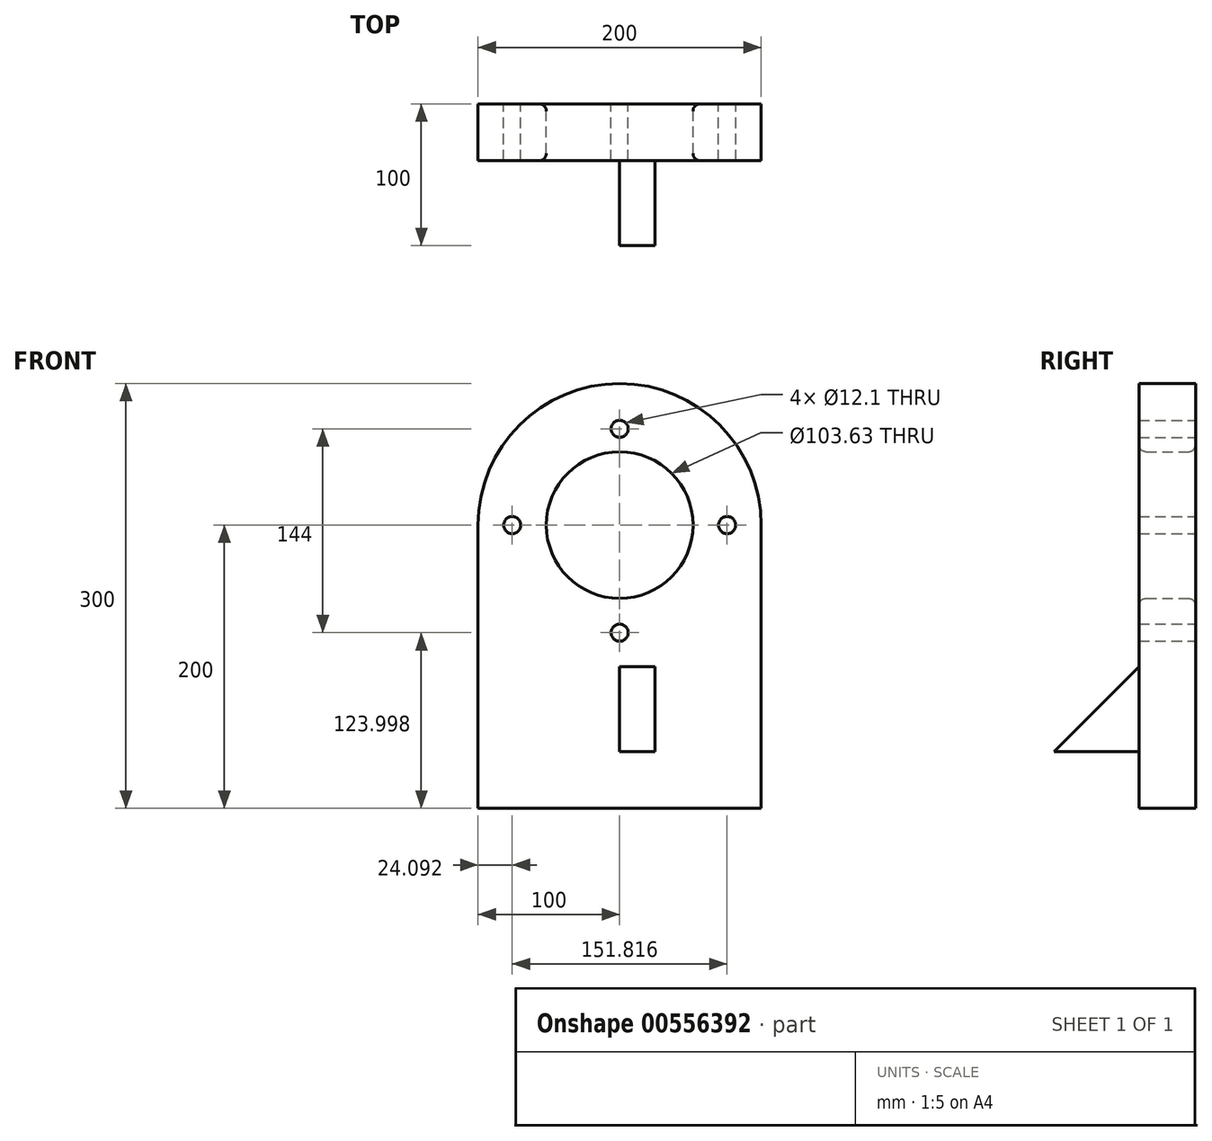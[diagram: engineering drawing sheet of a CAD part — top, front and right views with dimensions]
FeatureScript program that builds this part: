
annotation { "Feature Type Name" : "Feature", "Feature Type Description" : "" }
export const myFeature = defineFeature(function(context is Context, id is Id, definition is map)
    precondition{}
    {
        {
            var Q0;
            Q0=qCreatedBy(makeId("Front.planeOp"),FACE);
            var sketch = newSketch(context, id + "F0", { "sketchPlane" : qUnion([Q0])});
            skLineSegment(sketch, "E0.bottom", {"start": v(0, 0) * mm, "end": v(-100, 0) * mm});
            skLineSegment(sketch, "E0.top", {"start": v(-51.82, 200) * mm, "end": v(-100, 200) * mm});
            skLineSegment(sketch, "E0.left", {"start": v(0, 0) * mm, "end": v(0, 148.18) * mm});
            skLineSegment(sketch, "E0.right", {"start": v(-100, 0) * mm, "end": v(-100, 200) * mm});
            skLineSegment(sketch, "E1.MirrorCS", {"start": v(0, 0) * mm, "end": v(100, 0) * mm});
            skLineSegment(sketch, "E2.MirrorCS", {"start": v(100, 0) * mm, "end": v(100, 200) * mm});
            skLineSegment(sketch, "E3.MirrorCS", {"start": v(51.82, 200) * mm, "end": v(100, 200) * mm});
            skCircle(sketch, "E4", {"center": v(0, 200) * mm, "radius": 100 * mm});
            skCircle(sketch, "E5", {"center": v(0, 200) * mm, "radius": 51.82 * mm});
            skPoint(sketch, "E6", {"position": v(-75.9, 200) * mm});
            skPoint(sketch, "E7", {"position": v(0, 268) * mm});
            skPoint(sketch, "E8", {"position": v(75.9, 200) * mm});
            skPoint(sketch, "E9", {"position": v(0, 124) * mm});
            skLineSegment(sketch, "E10", {"start": v(0, 148.18) * mm, "end": v(0, 351.78) * mm});
            skSolve(sketch);
        }
        {
            var Q0;
            {var subQ0=sQuery(id+"F0.wireOp",EDGE,"E0.bottom");Q0=makeQuery(id+"F0.imprint","IMPRINT",FACE,{"disambiguationData":[TD([[makeQuery(id+"F0.imprint","IMPRINT",EDGE,{"derivedFrom":subQ0}),-1.0]])]});}
            var Q1;
            {var subQ0=sQuery(id+"F0.wireOp",EDGE,"E1.MirrorCS");Q1=makeQuery(id+"F0.imprint","IMPRINT",FACE,{"disambiguationData":[TD([[makeQuery(id+"F0.imprint","IMPRINT",EDGE,{"derivedFrom":subQ0}),1.0]])]});}
            var Q2;
            {var subQ0=sQuery(id+"F0.wireOp",EDGE,"E10");var subQ1=sQuery(id+"F0.wireOp",EDGE,"E0.left");var subQ2=makeQuery(id+"F0.imprint","INTERSECT",VERTEX,{"derivedFrom":[subQ1,subQ0]});Q2=makeQuery(id+"F0.imprint","IMPRINT",FACE,{"disambiguationData":[TD([[makeQuery(id+"F0.imprint","IMPRINT",EDGE,{"disambiguationData":[TD([[subQ2,1.0]])],"derivedFrom":subQ1}),1.0]])]});}
            var Q3;
            {var subQ0=sQuery(id+"F0.wireOp",EDGE,"E10");var subQ1=sQuery(id+"F0.wireOp",EDGE,"E0.left");var subQ2=makeQuery(id+"F0.imprint","INTERSECT",VERTEX,{"derivedFrom":[subQ1,subQ0]});Q3=makeQuery(id+"F0.imprint","IMPRINT",FACE,{"disambiguationData":[TD([[makeQuery(id+"F0.imprint","IMPRINT",EDGE,{"disambiguationData":[TD([[subQ2,1.0]])],"derivedFrom":subQ1}),-1.0]])]});}
            var Q4;
            {var subQ0=sQuery(id+"F0.wireOp",EDGE,"E0.top");Q4=makeQuery(id+"F0.imprint","IMPRINT",FACE,{"disambiguationData":[TD([[makeQuery(id+"F0.imprint","IMPRINT",EDGE,{"derivedFrom":subQ0}),-1.0]])]});}
            var Q5;
            {var subQ0=sQuery(id+"F0.wireOp",EDGE,"E3.MirrorCS");Q5=makeQuery(id+"F0.imprint","IMPRINT",FACE,{"disambiguationData":[TD([[makeQuery(id+"F0.imprint","IMPRINT",EDGE,{"derivedFrom":subQ0}),1.0]])]});}
            extrude(context, id + "F1", {"entities" : qUnion([Q0, Q1, Q2, Q3, Q4, Q5]), "depth" : 40 * mm, "offsetDistance" : 25 * mm});
        }
        {
            var Q0;
            Q0=sQuery(id+"F0.wireOp",VERTEX,"E6");
            var Q1;
            Q1=sQuery(id+"F0.wireOp",VERTEX,"E7");
            var Q2;
            Q2=sQuery(id+"F0.wireOp",VERTEX,"E8");
            var Q3;
            Q3=sQuery(id+"F0.wireOp",VERTEX,"E9");
            var Q4;
            Q4=makeQuery(id+"F1.opExtrude","SWEPT_BODY",BODY,{"disambiguationData":[OSD([sQuery(id+"F0.wireOp",EDGE,"E0.bottom"),sQuery(id+"F0.wireOp",EDGE,"E0.right"),sQuery(id+"F0.wireOp",EDGE,"E1.MirrorCS"),sQuery(id+"F0.wireOp",EDGE,"E2.MirrorCS"),sQuery(id+"F0.wireOp",EDGE,"E4")])]});
            hole(context, id + "F2", {"style" : HoleStyle.SIMPLE, "endStyle" : HoleEndStyle.THROUGH, "oppositeDirection" : true, "standardTappedOrClearance" : lookupTablePath({ "standard" : "ISO", "engagement" : "75%", "pitch" : "2 mm", "size" : "M14", "type" : "Tapped" }), "standardBlindInLast" : lookupTablePath({ "standard" : "ISO", "engagement" : "75%", "pitch" : "2 mm", "size" : "M14", "type" : "Tapped" }), "holeDiameter" : 12.1 * mm, "showTappedDepth" : true, "isTappedThrough" : true, "tappedDepth" : 12 * mm, "tapClearance" : 3, "locations" : qUnion([Q0, Q1, Q2, Q3]), "scope" : qUnion([Q4]), "majorDiameter" : 14 * mm});
        }
        {
            var Q0;
            Q0=makeQuery(id+"F1.opExtrude","CAP_EDGE",EDGE,{"disambiguationData":[OSD([sQuery(id+"F0.wireOp",EDGE,"E5")])],"isStart":false});
            fillet(context, id + "F3", {"entities" : qUnion([Q0]), "radius" : 5 * mm, "tangentPropagation" : true, "allowEdgeOverflow" : false});
        }
        {
            var Q0;
            Q0=makeQuery(id+"F1.opExtrude","CAP_EDGE",EDGE,{"disambiguationData":[OSD([sQuery(id+"F0.wireOp",EDGE,"E5")])],"isStart":true});
            fillet(context, id + "F4", {"entities" : qUnion([Q0]), "radius" : 5 * mm, "tangentPropagation" : true, "allowEdgeOverflow" : false});
        }
        {
            var Q0;
            Q0=qCreatedBy(makeId("Right.planeOp"),FACE);
            var sketch = newSketch(context, id + "F5", { "sketchPlane" : qUnion([Q0])});
            skLineSegment(sketch, "E11.bottom", {"start": v(-40, 40) * mm, "end": v(-100, 40) * mm});
            skLineSegment(sketch, "E12", {"start": v(-40, 40) * mm, "end": v(-40, 100) * mm});
            skLineSegment(sketch, "E13", {"start": v(-100, 40) * mm, "end": v(-40, 100) * mm});
            skPoint(sketch, "E14.bottom.end.orphan", {"position": v(-100, 0) * mm});
            skPoint(sketch, "E11.left.start.orphan", {"position": v(0, 40) * mm});
            skPoint(sketch, "E15.orphan", {"position": v(0, 0) * mm});
            skPoint(sketch, "E14.left.end.orphan", {"position": v(0, 100) * mm});
            skLineSegment(sketch, "E16", {"start": v(-40, 100) * mm, "end": v(-40, 40) * mm});
            skSolve(sketch);
        }
        {
            var Q0;
            Q0=makeQuery(id+"F5.imprint","IMPRINT",FACE,{"disambiguationData":[TD([[makeQuery(id+"F5.imprint","IMPRINT",EDGE,{"derivedFrom":sQuery(id+"F5.wireOp",EDGE,"E11.bottom")}),-1.0]])]});
            extrude(context, id + "F6", {"entities" : qUnion([Q0]), "operationType" : NewBodyOperationType.ADD, "depth" : 25 * mm, "offsetDistance" : 25 * mm});
        }
    });
